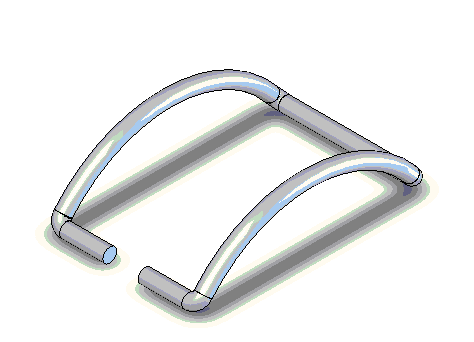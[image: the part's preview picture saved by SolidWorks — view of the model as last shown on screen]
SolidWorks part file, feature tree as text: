
SOLIDWORKS PART (.sldprt)
format: sldprt  version: not decoded by parser v0  size: 463,360 bytes
history: native  units: mm
features: sketch x8, plane x4, sweep x1, cut_extrude x1 (+11 scaffold rows collapsed)
feature tree (25):
  scaffold x11  (default folders/planes/origin — collapsed)
  plane  "Plane1"  Offset=9.9mm
  plane  "Plane2"  Offset=9.9mm
  sketch  "Sketch1"  dims[c1.D3=1.25mm c1.D1=31.0mm c1.D2=11.45mm c2.D3=20.2mm c2.D4=10.1mm]
  plane  "Plane3"
  plane  "Plane4"
  sketch  "Sketch5"  dims[D1=2.5mm]
  sketch  "Sketch6"  dims[D1=2.5mm]
  sketch  "Sketch7"  dims[D1=7.1mm]
  sketch  "Sketch8"
  sketch  "Sketch9"  dims[D1=2.0mm]
  sketch  "3DSketch4"
  sweep  "Sweep6"
  sketch  "Sketch10"  dims[D1=5.0mm]
  cut_extrude  "Cut-Extrude1"  [1 undecoded]
decode coverage: 6 of 10 modeling features carry decoded parameters
note: 1 parameter value undecoded
note: suppression state not decoded; provenance and decode notes live in map.json
